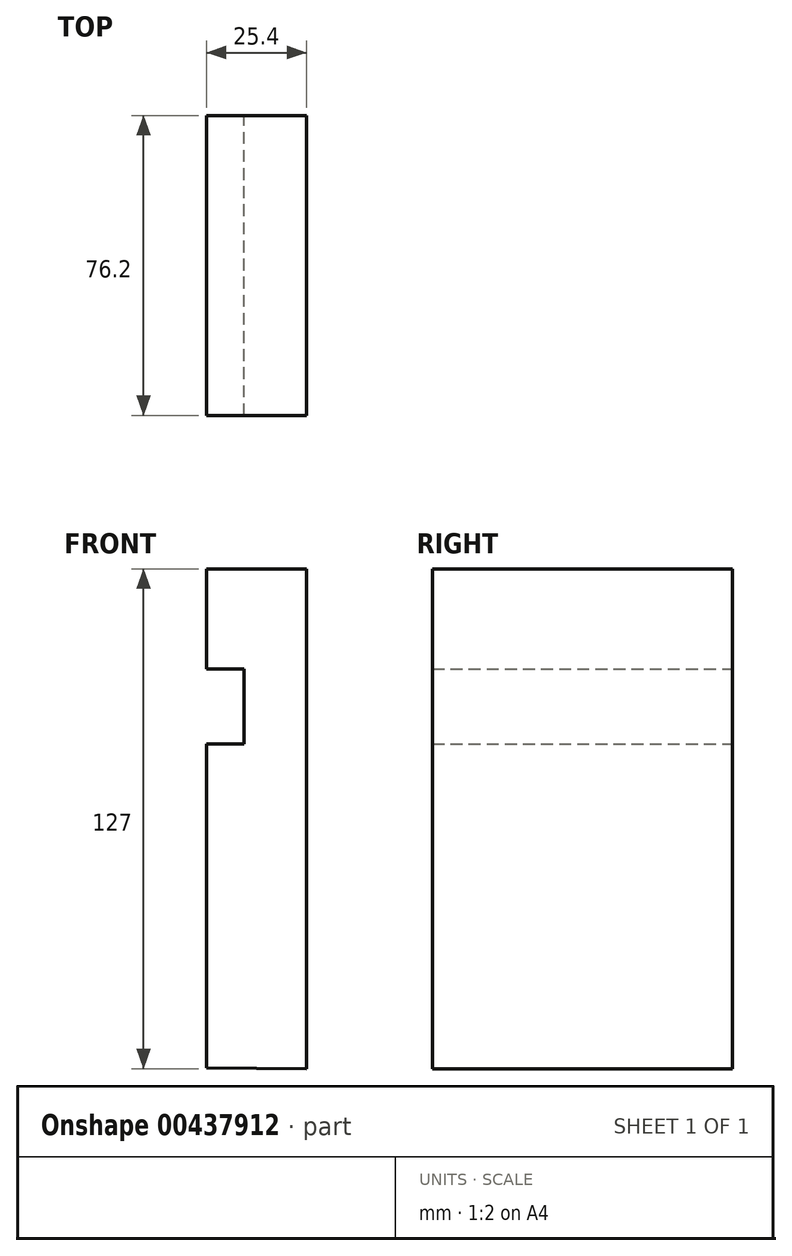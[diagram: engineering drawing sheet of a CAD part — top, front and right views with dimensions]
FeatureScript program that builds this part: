
annotation { "Feature Type Name" : "Feature", "Feature Type Description" : "" }
export const myFeature = defineFeature(function(context is Context, id is Id, definition is map)
    precondition{}
    {
        {
            var Q0;
            Q0=qCreatedBy(makeId("Front.planeOp"),FACE);
            var sketch = newSketch(context, id + "F0", { "sketchPlane" : qUnion([Q0])});
            skLineSegment(sketch, "E0", {"start": v(0, -70.86) * mm, "end": v(0, 56.14) * mm});
            skLineSegment(sketch, "E1", {"start": v(0, 56.14) * mm, "end": v(-25.4, 56.14) * mm});
            skLineSegment(sketch, "E2", {"start": v(-25.4, 56.14) * mm, "end": v(-25.4, 30.74) * mm});
            skLineSegment(sketch, "E3", {"start": v(-25.4, 30.74) * mm, "end": v(-15.87, 30.74) * mm});
            skLineSegment(sketch, "E4", {"start": v(-15.87, 30.74) * mm, "end": v(-15.87, 11.7) * mm});
            skLineSegment(sketch, "E5", {"start": v(-15.87, 11.7) * mm, "end": v(-25.4, 11.7) * mm});
            skLineSegment(sketch, "E6", {"start": v(-25.4, 11.7) * mm, "end": v(-25.4, -70.65) * mm});
            skLineSegment(sketch, "E7", {"start": v(-25.4, -70.65) * mm, "end": v(0, -70.86) * mm});
            skSolve(sketch);
        }
        {
            var Q0;
            Q0 = qSketchRegion(id + "F0", true);
            extrude(context, id + "F1", {"entities" : qUnion([Q0]), "depth" : 76.2 * mm});
        }
    });
